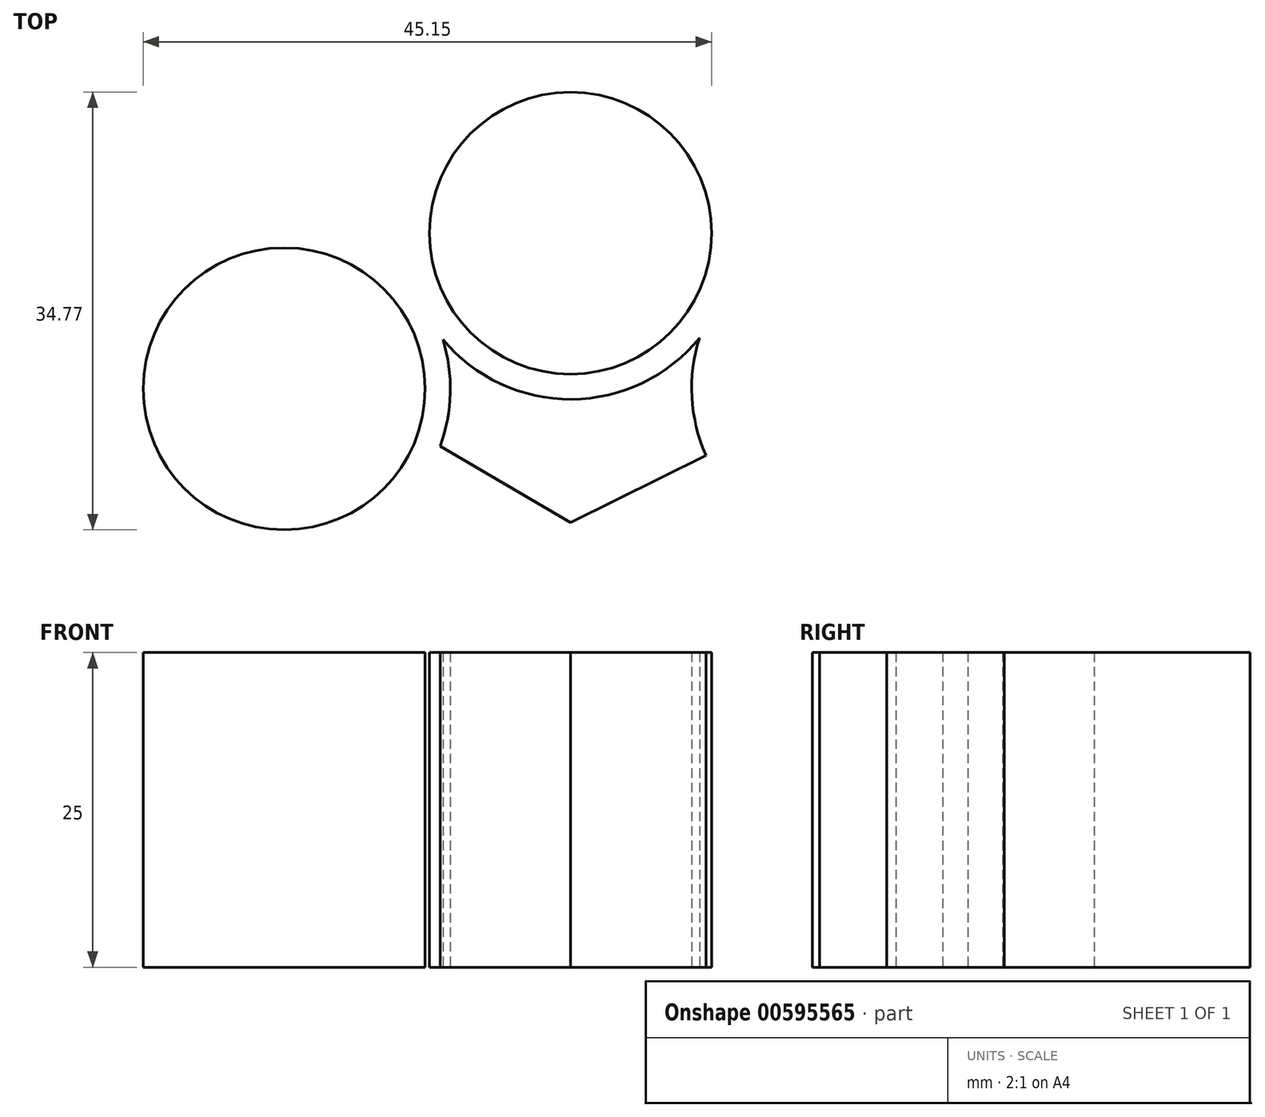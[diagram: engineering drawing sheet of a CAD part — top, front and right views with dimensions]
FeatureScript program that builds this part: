
annotation { "Feature Type Name" : "Feature", "Feature Type Description" : "" }
export const myFeature = defineFeature(function(context is Context, id is Id, definition is map)
    precondition{}
    {
        {
            var Q0;
            Q0=qCreatedBy(makeId("Top.planeOp"),FACE);
            var sketch = newSketch(context, id + "F0", { "sketchPlane" : qUnion([Q0])});
            skCircle(sketch, "E0", {"center": v(0, 0) * mm, "radius": 11.2 * mm});
            skCircle(sketch, "E1", {"center": v(0, 0) * mm, "radius": 13.2 * mm});
            skCircle(sketch, "E2", {"center": v(0, 27.12) * mm, "radius": 11.2 * mm});
            skCircle(sketch, "E3", {"center": v(0, 27.12) * mm, "radius": 13.2 * mm});
            skCircle(sketch, "E4.1.0", {"center": v(-22.75, -12.37) * mm, "radius": 13.2 * mm});
            skCircle(sketch, "E4.1.1", {"center": v(-22.75, -12.37) * mm, "radius": 11.2 * mm});
            skCircle(sketch, "E4.2.0", {"center": v(22.82, -12.32) * mm, "radius": 13.2 * mm});
            skCircle(sketch, "E4.2.1", {"center": v(22.82, -12.32) * mm, "radius": 11.2 * mm});
            skPoint(sketch, "E4.center", {"position": v(0.03, 0.8) * mm});
            skLineSegment(sketch, "E5", {"start": v(-10.36, -16.94) * mm, "end": v(0, -23) * mm});
            skLineSegment(sketch, "E6", {"start": v(10.75, -17.66) * mm, "end": v(0, -23) * mm});
            skLineSegment(sketch, "E7.1.0", {"start": v(19.85, -0.5) * mm, "end": v(19.91, 11.5) * mm});
            skLineSegment(sketch, "E7.1.1", {"start": v(9.92, 18.14) * mm, "end": v(19.91, 11.5) * mm});
            skLineSegment(sketch, "E7.2.0", {"start": v(-9.49, 17.44) * mm, "end": v(-19.91, 11.5) * mm});
            skLineSegment(sketch, "E7.2.1", {"start": v(-20.67, -0.48) * mm, "end": v(-19.91, 11.5) * mm});
            skSolve(sketch);
        }
        {
            var Q0;
            Q0=makeQuery(id+"F0.imprint","IMPRINT",FACE,{"disambiguationData":[TD([[makeQuery(id+"F0.imprint","IMPRINT",EDGE,{"derivedFrom":sQuery(id+"F0.wireOp",EDGE,"E4.1.1")}),1.0]])]});
            var Q1;
            {var subQ0=sQuery(id+"F0.wireOp",EDGE,"E5");Q1=makeQuery(id+"F0.imprint","IMPRINT",FACE,{"disambiguationData":[TD([[makeQuery(id+"F0.imprint","IMPRINT",EDGE,{"derivedFrom":subQ0}),1.0]])]});}
            var Q2;
            Q2=makeQuery(id+"F0.imprint","IMPRINT",FACE,{"disambiguationData":[TD([[makeQuery(id+"F0.imprint","IMPRINT",EDGE,{"derivedFrom":sQuery(id+"F0.wireOp",EDGE,"E0")}),1.0]])]});
            extrude(context, id + "F1", {"entities" : qUnion([Q0, Q1, Q2]), "depth" : 25 * mm, "offsetDistance" : 25 * mm});
        }
    });
